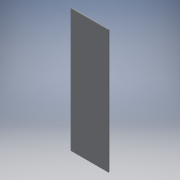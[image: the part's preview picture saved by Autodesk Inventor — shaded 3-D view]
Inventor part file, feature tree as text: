
AUTODESK INVENTOR PART (.ipt)
format: ipt  version: 2016 (Build 200138000, 138)  size: 90,624 bytes
history: native  units: mm
features: extrude x1, sketch x1
ambient origin geometry x8: Origin, YZ Plane, XZ Plane, XY Plane, X Axis, Y Axis, Z Axis, Center Point
bodies: Solid1 (feature_tree)
feature tree (2):
  extrude  "Extrusion1"  Depth=220.0mm
  sketch  "Sketch1"  dims[d0=720.0mm d1=220.0mm d2=5.0mm d3=0.0mm]
